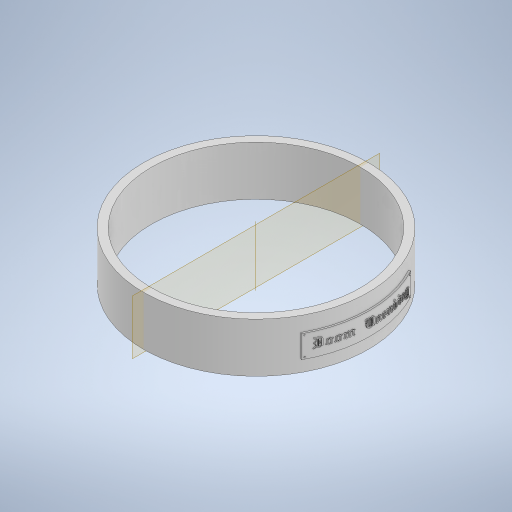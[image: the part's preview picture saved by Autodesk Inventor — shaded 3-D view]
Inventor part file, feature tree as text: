
AUTODESK INVENTOR PART (.ipt)
format: ipt  version: 2023 (Build 270158000, 158)  size: 5,312,000 bytes
history: native  units: in
note: dims shown in document units (in); Inventor stores cm internally (conversion verified against a paired STEP export)
features: emboss x3, pattern_circular x3, other x2, extrude x1, plane x1, fillet x1, sketch x1
ambient origin geometry x8: Origin, YZ Plane, XZ Plane, XY Plane, X Axis, Y Axis, Z Axis, Center Point
bodies: Solid1 (feature_tree)
feature tree (12):
  extrude  "Extrusion1"  Depth=1.9685in
  plane  "Work Plane1"
  other  "Text"
  emboss  "Emboss4"
  emboss  "Emboss5"
  emboss  "Emboss6"
  fillet  "Rivots"  Radius=0.8661in
  pattern_circular  "Circular Pattern1"  Count=6  [1 undecoded]
  pattern_circular  "Circular Pattern2"  [2 undecoded]
  pattern_circular  "Circular Pattern3"  [2 undecoded]
  sketch  "Sketch1"  dims[d0=3.937in d1=3.6614in d2=0.8661in d3=0.0in d4=2.3622in d6=0.4546in d10=0.0in d11=0.3937in d12=1.9685in d19=0.0in d20=0.0in d21=0.0295in d22=0.0in d23=0.0197in d24=0.0in d25=0.0295in d26=0.0295in d27=0.0295in d28=0.0157in d29=0.0in d30=0.0138in d31=0.7874in d32=360.0deg d34=0.7874in d35=360.0deg d37=0.7874in d38=360.0deg d33=0.0in]
  other  "NamePlate"
note: 5 required parameter values undecoded (feature->parameter linkage not recoverable at this tier; creation-order binding heuristic only, values carry confidence <= 0.55)
